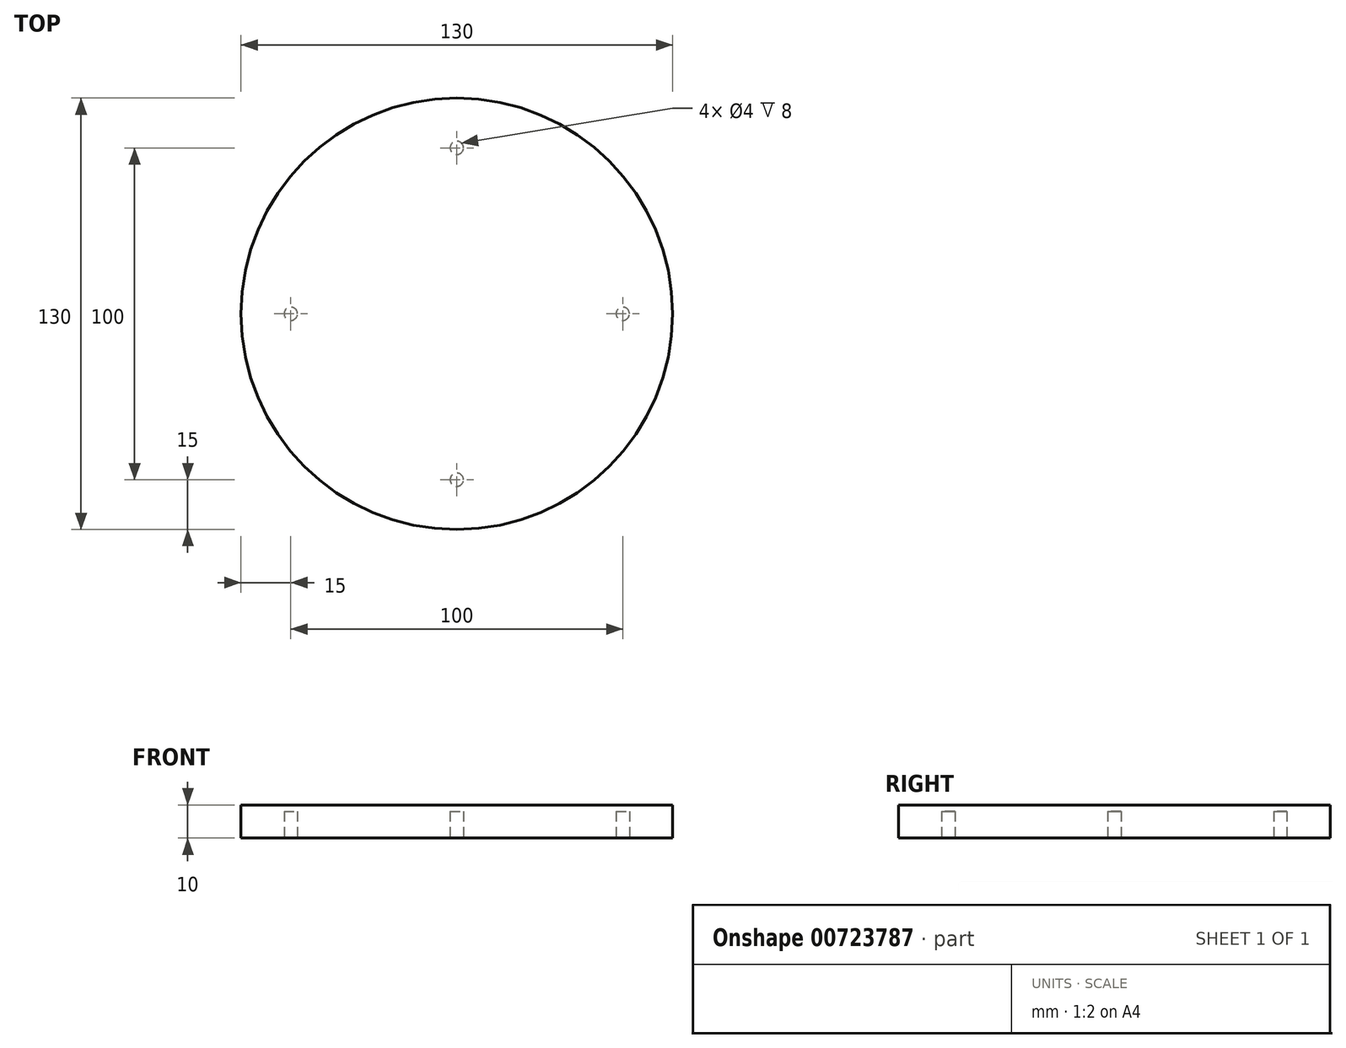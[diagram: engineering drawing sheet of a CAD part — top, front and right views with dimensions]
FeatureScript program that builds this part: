
annotation { "Feature Type Name" : "Feature", "Feature Type Description" : "" }
export const myFeature = defineFeature(function(context is Context, id is Id, definition is map)
    precondition{}
    {
        {
            var Q0;
            Q0=qCreatedBy(makeId("Top.planeOp"),FACE);
            var sketch = newSketch(context, id + "F0", { "sketchPlane" : qUnion([Q0])});
            skCircle(sketch, "E0", {"center": v(0, 0) * mm, "radius": 65 * mm});
            skSolve(sketch);
        }
        {
            var Q0;
            Q0=makeQuery(id+"F0.imprint","IMPRINT",FACE,{"disambiguationData":[TD([[makeQuery(id+"F0.imprint","IMPRINT",EDGE,{"derivedFrom":sQuery(id+"F0.wireOp",EDGE,"E0")}),1.0]])]});
            extrude(context, id + "F1", {"entities" : qUnion([Q0]), "depth" : 10 * mm, "offsetDistance" : 25 * mm});
        }
        {
            var Q0;
            Q0=makeQuery(id+"F1.opExtrude","CAP_FACE",FACE,{"disambiguationData":[OSD([sQuery(id+"F0.wireOp",EDGE,"E0")])],"isStart":true});
            var sketch = newSketch(context, id + "F2", { "sketchPlane" : qUnion([Q0])});
            skLineSegment(sketch, "E1", {"start": v(0, 0) * mm, "end": v(0, 50) * mm, "construction": true});
            skCircle(sketch, "E2", {"center": v(0, 50) * mm, "radius": 2 * mm});
            skCircle(sketch, "E3.1.0", {"center": v(50, 0) * mm, "radius": 2 * mm});
            skCircle(sketch, "E3.2.0", {"center": v(0, -50) * mm, "radius": 2 * mm});
            skCircle(sketch, "E3.3.0", {"center": v(-50, 0) * mm, "radius": 2 * mm});
            skPoint(sketch, "E3.center", {"position": v(0, 0) * mm});
            skLineSegment(sketch, "E3.anchor2", {"start": v(0, 0) * mm, "end": v(-50, 0) * mm, "construction": true});
            skSolve(sketch);
        }
        {
            var Q0;
            Q0=qSketchRegion(id+"F2",true);
            extrude(context, id + "F3", {"entities" : qUnion([Q0]), "operationType" : NewBodyOperationType.REMOVE, "oppositeDirection" : true, "depth" : 8 * mm, "offsetDistance" : 25 * mm});
        }
    });
